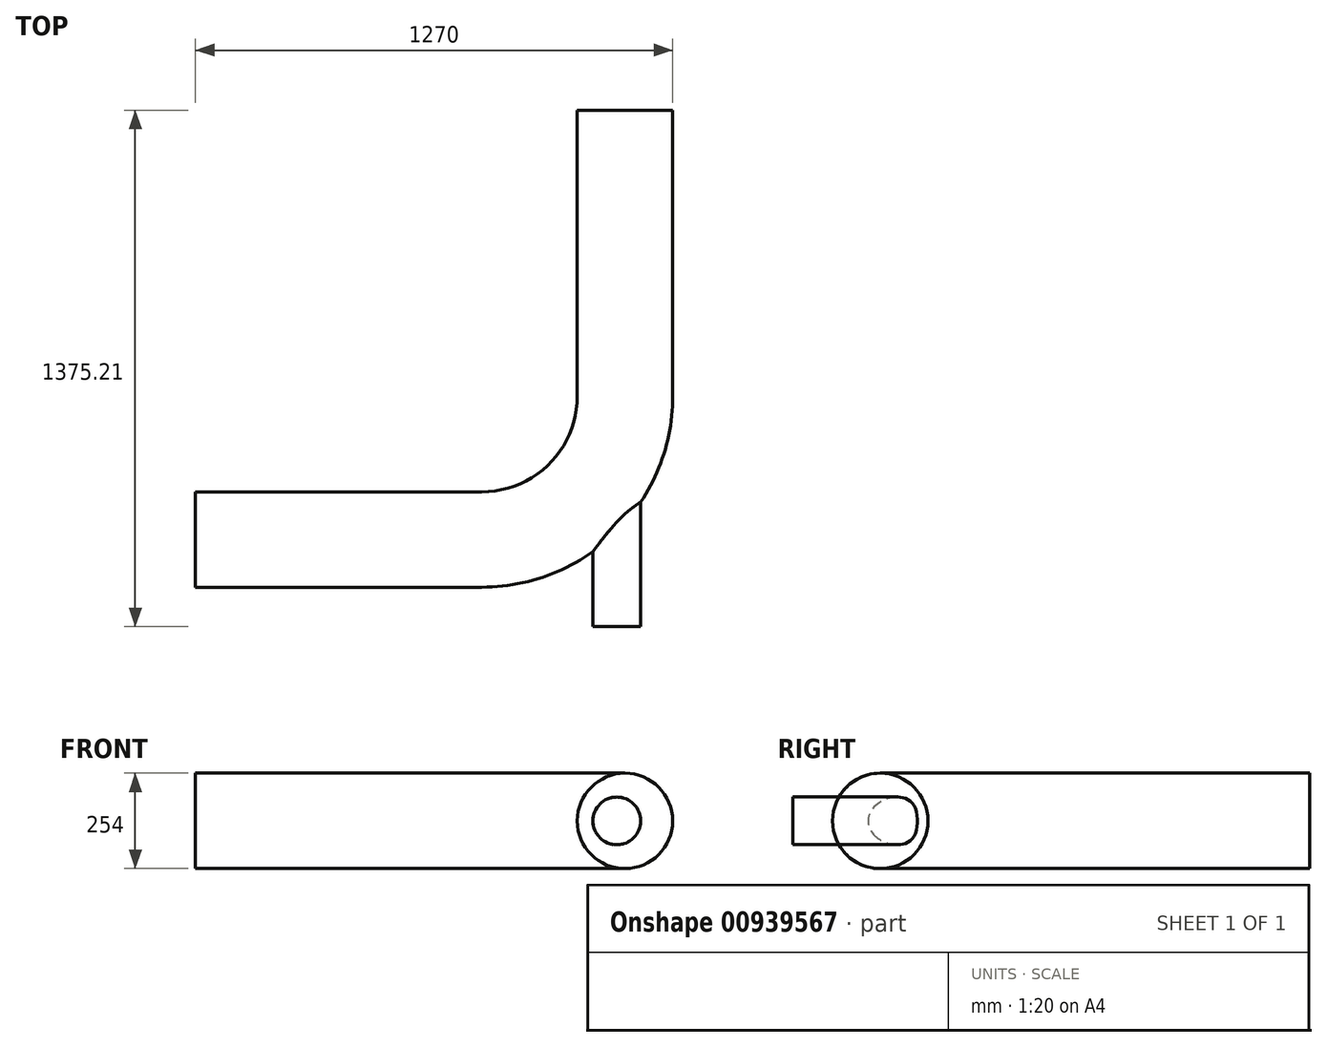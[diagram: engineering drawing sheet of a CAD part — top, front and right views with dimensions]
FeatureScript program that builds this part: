
annotation { "Feature Type Name" : "Feature", "Feature Type Description" : "" }
export const myFeature = defineFeature(function(context is Context, id is Id, definition is map)
    precondition{}
    {
        {
            var Q0;
            Q0=qCreatedBy(makeId("Top.planeOp"),FACE);
            var sketch = newSketch(context, id + "F0", { "sketchPlane" : qUnion([Q0])});
            skLineSegment(sketch, "E0", {"start": v(0, 0) * mm, "end": v(762, 0) * mm});
            skArc(sketch, "E1", {"start": v(762, 0) * mm, "mid": v(1031.4, 111.6) * mm, "end": v(1143, 381) * mm});
            skLineSegment(sketch, "E2", {"start": v(1143, 381) * mm, "end": v(1143, 1143) * mm});
            skArc(sketch, "E3.1", {"start": v(762, -127) * mm, "mid": v(1121.21, 21.79) * mm, "end": v(1270, 381) * mm, "construction": true});
            skLineSegment(sketch, "E4", {"start": v(762, 381) * mm, "end": v(762, -127) * mm, "construction": true});
            skLineSegment(sketch, "E5", {"start": v(762, 381) * mm, "end": v(1121.21, 21.79) * mm, "construction": true});
            skLineSegment(sketch, "E6", {"start": v(1121.21, 21.79) * mm, "end": v(1121.21, -232.21) * mm});
            skSolve(sketch);
        }
        {
            var Q0;
            Q0=qCreatedBy(makeId("Right.planeOp"),FACE);
            var sketch = newSketch(context, id + "F1", { "sketchPlane" : qUnion([Q0])});
            skCircle(sketch, "E7", {"center": v(0, 0) * mm, "radius": 127 * mm});
            skSolve(sketch);
        }
        {
            var Q0;
            Q0=makeQuery(id+"F1.imprint","IMPRINT",FACE,{"disambiguationData":[TD([[makeQuery(id+"F1.imprint","IMPRINT",EDGE,{"derivedFrom":sQuery(id+"F1.wireOp",EDGE,"E7")}),1.0]])]});
            var Q1;
            Q1 = qSketchRegion(id + "F0", true);
            var Q2;
            Q2=sQuery(id+"F0.wireOp",EDGE,"E0");
            var Q3;
            Q3=sQuery(id+"F0.wireOp",EDGE,"E1");
            var Q4;
            Q4=sQuery(id+"F0.wireOp",EDGE,"E2");
            sweep(context, id + "F2", {"profiles" : qUnion([Q0, Q1]), "path" : qUnion([Q2, Q3, Q4])});
        }
        {
            var Q0;
            Q0=sQuery(id+"F0.wireOp",VERTEX,"E6.end");
            var Q1;
            Q1=sQuery(id+"F0.wireOp",EDGE,"E6");
            cPlane(context, id + "F3", {"entities" : qUnion([Q0, Q1]), "cplaneType" : CPlaneType.LINE_POINT, "offset" : 25.4 * mm, "width" : 152.4 * mm, "height" : 152.4 * mm});
        }
        {
            var Q0;
            Q0=qCreatedBy(id+"F3.planeOp",FACE);
            var sketch = newSketch(context, id + "F4", { "sketchPlane" : qUnion([Q0])});
            skPoint(sketch, "E8.0", {"position": v(1121.21, 0) * mm});
            skCircle(sketch, "E9", {"center": v(1121.21, 0) * mm, "radius": 63.5 * mm});
            skSolve(sketch);
        }
        {
            var Q0;
            Q0=makeQuery(id+"F4.imprint","IMPRINT",FACE,{"disambiguationData":[TD([[makeQuery(id+"F4.imprint","IMPRINT",EDGE,{"derivedFrom":sQuery(id+"F4.wireOp",EDGE,"E9")}),1.0]])]});
            extrude(context, id + "F5", {"entities" : qUnion([Q0]), "operationType" : NewBodyOperationType.ADD, "oppositeDirection" : true, "depth" : 558.8 * mm, "offsetDistance" : 25.4 * mm});
        }
    });
